# Revit family: 40-30408 - Mobilio changing bed 160cm + bedguard
name_source: partatom
category: Furniture
units: mm (PartAtom-declared; Revit-internal decimal feet)

## family parameters
Always vertical = Yes
Cut with Voids When Loaded = No
Enable Cutting in Views = Yes
OmniClass Number = 0.0.0.0
Render Appearance Source = Family Geometry
Room Calculation Point = No
Shared = No
Work Plane-Based = No

## types (1)
- Standard
    Cost Center = 0 g
    Default Elevation = 0 mm  [stored 0 ft]
    Description = Mobilio skifteleje 160cm
    Design State = 1
    Designer = sj
    Height = 0 mm  [stored 0 ft]
    L = 1 mm  [stored 0.00328084 ft]
    Length = 0*10
    Malermeter = 192.522489
    Manufacturer = Ropox
    Model = 40-30408
    Part Number = 40-30411-5_Simplify_3
    SaveDate = 16-07-2008
    SaveTime = 09:39
    Width = 0*10

note: [stored X ft] marks values corroborated as IEEE doubles in the binary element streams (Revit-internal decimal feet)

## geometry (parser evidence)
native form markers: Sweep x3
no freeform markers — native parametric forms only
